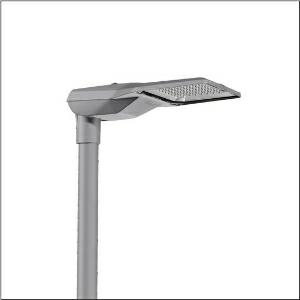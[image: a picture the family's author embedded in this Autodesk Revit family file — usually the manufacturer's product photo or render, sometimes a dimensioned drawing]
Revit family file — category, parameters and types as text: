
# Revit family: streetlight_sl_21_midi___st0_8a_5xe3c43s08mb_603c
name_source: partatom
category: Lighting Fixtures
units: mm (PartAtom-declared; Revit-internal decimal feet)

## family parameters
Cut with Voids When Loaded = No
Host = Face
Light Source = No
Part Type = Normal
Room Calculation Point = No
Round Connector Dimension = Use Diameter
Shared = No

## types (1)
- --- (1 x LED, 20180 lm, 147 W, 4000K)
    Apparent Load = 147 VA
    CIE Flux Codes = 38 75 97 100 100
    Color Rendering = 70
    Color Temperature = 4000K
    Default Elevation = 1800 mm
    Description = Streetlight SL 21 midi, mast luminaire, primary light control with lens, of PMMA, primary optical cover: cover, of toughened safety glass, transparent, light distribution: ST0.8a, light emission: direct distribution, primary light characteristic: asymmetric, installation type: side-entry, post-top, LED, High Power LED, rated luminous flux: 20.180lm, luminous efficacy: 137lm/W, light colour: 740, colour temperature: 4000K, control gear: D4i, control: overheat protection, constant luminous flux control, time-dependent luminous flux control, flexible luminous flux parameterisation, pre-setting: logarithmic dimming characteristic, mains connection: 230..240V, AC, 50/60Hz, start of lifetime: 147W, end of service life: 155W, reduction: 65W, luminaire housing, of diecast aluminium, powder-coated, Siteco® metallic grey (DB 702S), corrosivity category C5 mid according to DIN EN ISO 12944, please order mast flange separately, inclination adjustable: 0°, 5°, 10°, 15°, sealing non-destructively replaceable, multi-level sealing system, length: 644mm, width: 335mm, height: 110mm, mast flange for spigot size: 42mm (side-entry): 5XC10008XM4, 60/48mm (side-entry/post-top): 5XC10108XM2, 76/60mm (side-entry/post-top): 5XC10108XM1, mounting height: 4..8m, Smart Interface above, protection rating (complete): IP66, insulation class (complete): insulation class II (safety insulation), certification: CE, ENEC, ENEC+, VDE, impact resistance: IK10, permissible operating ambient temperature for outdoor applications: -40..+50°C, standard-compliant lighting for roads and squares, packaging unit: 1 piece

Light Distribution: ST0.8a
    Height = 111 mm
    Lamp = 1 x LED
    Lamp Light Flux = 20180 lm
    Lamp Power = 147 W
    Lamp count = 1
    Length = 644 mm
    Luminous efficacy = 137 lm/W
    Manufacturer = Siteco
    ModVariant = No
    Model = 5XE3C43S08MB
    Number of Poles = 1
    OnlyDefault = Yes
    Power Factor = 1
    Product Name = Streetlight SL 21 midi | ST0.8a
    Product group = mast luminaire | pylon top
    ProductGroupID = 6100
    Protection Class = Protection class II
    Protection Degree = IP 66
    RLX_Detail_Level = 1
    RLX_Emergency_Light_Flux = 0 lm
    RLX_Emergency_Type = 0
    RLX_Emergency_Type_DB = No
    RlxData = <blob elided: 26965 chars, md5=8fad2084>
    Socket = socket
    Standby Power = 0 W
    System Light Flux = 20180 lm
    System Power = 147 W
    Type Comments = factory setting: luminous flux: 100 % | dim-lin: 254 | 750 mA
    Type Image = l_1004302.jpg
    URL = http://relux.com
    VarID = @adj_207367
    Voltage = 0 V
    Weight = 0.00 kg
    Width = 336 mm

## geometry (parser evidence)
native form markers: Blend x4, Sweep x11
no freeform markers — native parametric forms only
